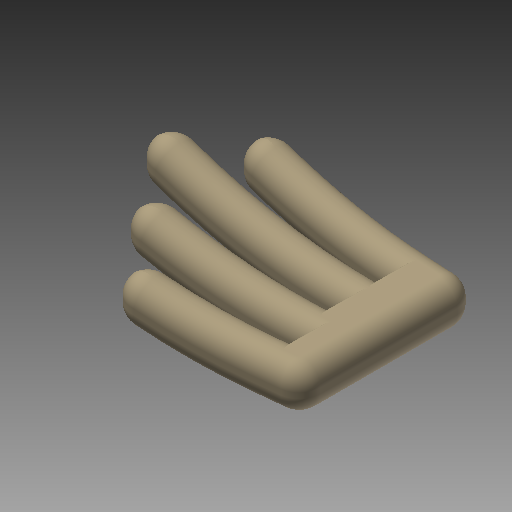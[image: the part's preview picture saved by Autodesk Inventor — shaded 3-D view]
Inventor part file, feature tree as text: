
AUTODESK INVENTOR PART (.ipt)
format: ipt  version: 2022 (Build 260153000, 153)  size: 636,416 bytes
history: native  units: mm (DEFAULTED — no unit token found)
features: other x3, plane x1
ambient origin geometry x8: Origin, YZ Plane, XZ Plane, XY Plane, X Axis, Y Axis, Z Axis, Center Point
bodies: Solid1 (feature_tree)
feature tree (4):
  other  "iMan - FINGERS LEFT"
  plane  "Work Plane1"
  other  "Work Axis1"
  other  "Solid1::iMike - FINGERS LEFT.ipt"
